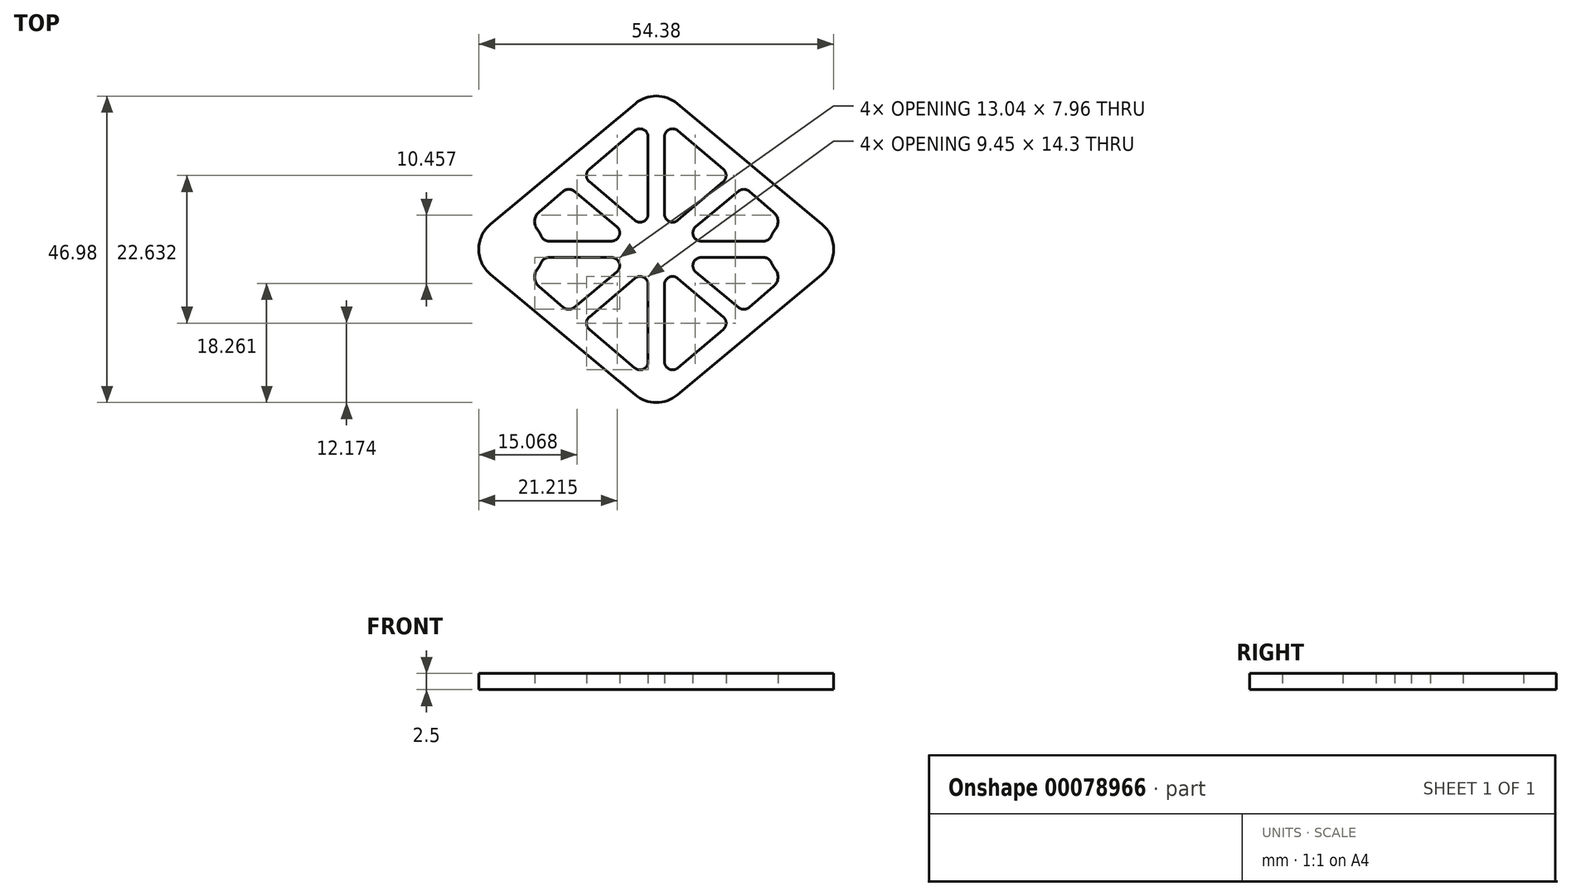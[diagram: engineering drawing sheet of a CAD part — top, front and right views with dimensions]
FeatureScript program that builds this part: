
annotation { "Feature Type Name" : "Feature", "Feature Type Description" : "" }
export const myFeature = defineFeature(function(context is Context, id is Id, definition is map)
    precondition{}
    {
        {
            var Q0;
            Q0=qCreatedBy(makeId("Top.planeOp"),FACE);
            var sketch = newSketch(context, id + "F0", { "sketchPlane" : qUnion([Q0])});
            skLineSegment(sketch, "E0.bottom", {"start": v(30, 25) * mm, "end": v(-30, 25) * mm, "construction": true});
            skLineSegment(sketch, "E0.top", {"start": v(30, -25) * mm, "end": v(-30, -25) * mm, "construction": true});
            skLineSegment(sketch, "E0.left", {"start": v(30, 25) * mm, "end": v(30, -25) * mm, "construction": true});
            skLineSegment(sketch, "E0.right", {"start": v(-30, 25) * mm, "end": v(-30, -25) * mm, "construction": true});
            skPoint(sketch, "E0.middle", {"position": v(0, 0) * mm});
            skPoint(sketch, "E1", {"position": v(0, 25) * mm});
            skPoint(sketch, "E2", {"position": v(0, -25) * mm});
            skPoint(sketch, "E3", {"position": v(30, 0) * mm});
            skPoint(sketch, "E4", {"position": v(-30, 0) * mm});
            skLineSegment(sketch, "E5", {"start": v(-25.4, 3.84) * mm, "end": v(-3.2, 22.33) * mm});
            skLineSegment(sketch, "E6", {"start": v(3.2, 22.33) * mm, "end": v(25.4, 3.84) * mm});
            skLineSegment(sketch, "E7", {"start": v(25.4, -3.84) * mm, "end": v(3.2, -22.33) * mm});
            skLineSegment(sketch, "E8", {"start": v(-3.2, -22.33) * mm, "end": v(-25.4, -3.84) * mm});
            skArc(sketch, "E9.filletArc", {"start": v(3.2, 22.33) * mm, "mid": v(0, 23.5) * mm, "end": v(-3.2, 22.33) * mm});
            skArc(sketch, "E10.filletArc", {"start": v(-25.4, 3.84) * mm, "mid": v(-27.19, 0) * mm, "end": v(-25.4, -3.84) * mm});
            skArc(sketch, "E11.filletArc", {"start": v(-3.2, -22.33) * mm, "mid": v(0, -23.5) * mm, "end": v(3.2, -22.33) * mm});
            skArc(sketch, "E12.filletArc", {"start": v(25.4, -3.84) * mm, "mid": v(27.19, 0) * mm, "end": v(25.4, 3.84) * mm});
            skCircle(sketch, "E13", {"center": v(-22.19, 0) * mm, "radius": 5 * mm});
            skPoint(sketch, "E14", {"position": v(-27.19, 0) * mm});
            skLineSegment(sketch, "E15", {"start": v(-22.19, 0) * mm, "end": v(-27.19, 0) * mm, "construction": true});
            skPoint(sketch, "E16", {"position": v(-24.69, 0) * mm});
            skPoint(sketch, "E17", {"position": v(0, 21) * mm});
            skPoint(sketch, "E18", {"position": v(-17.97, 5.71) * mm});
            skPoint(sketch, "E19", {"position": v(-18.24, 3.07) * mm});
            skArc(sketch, "E20", {"start": v(-17.97, 5.71) * mm, "mid": v(-18.64, 4.45) * mm, "end": v(-18.24, 3.07) * mm});
            skArc(sketch, "E21.MirrorCS", {"start": v(-17.97, -5.71) * mm, "mid": v(-18.64, -4.45) * mm, "end": v(-18.24, -3.07) * mm});
            skCircle(sketch, "E22", {"center": v(-22.19, 0) * mm, "radius": 2.5 * mm});
            skLineSegment(sketch, "E23", {"start": v(0, 0) * mm, "end": v(0, 21) * mm, "construction": true});
            skLineSegment(sketch, "E24.MirrorCS", {"start": v(24.69, 0) * mm, "end": v(0, 21) * mm, "construction": true});
            skArc(sketch, "E25.MirrorCS", {"start": v(17.97, 5.71) * mm, "mid": v(18.64, 4.45) * mm, "end": v(18.24, 3.07) * mm});
            skCircle(sketch, "E26.MirrorC", {"center": v(22.19, 0) * mm, "radius": 5 * mm});
            skCircle(sketch, "E27.MirrorC", {"center": v(22.19, 0) * mm, "radius": 2.5 * mm});
            skArc(sketch, "E28.MirrorCS", {"start": v(17.97, -5.71) * mm, "mid": v(18.64, -4.45) * mm, "end": v(18.24, -3.07) * mm});
            skLineSegment(sketch, "E29.MirrorCS", {"start": v(24.69, 0) * mm, "end": v(0, -21) * mm, "construction": true});
            skLineSegment(sketch, "E30", {"start": v(-17.97, 5.71) * mm, "end": v(0, 21) * mm, "construction": true});
            skLineSegment(sketch, "E31", {"start": v(-17.97, -5.71) * mm, "end": v(0, -21) * mm, "construction": true});
            skPoint(sketch, "E32", {"position": v(12.34, 10.5) * mm});
            skLineSegment(sketch, "E33", {"start": v(17.97, -5.71) * mm, "end": v(0, -21) * mm, "construction": true});
            skLineSegment(sketch, "E34", {"start": v(0, 0) * mm, "end": v(12.34, 10.5) * mm, "construction": true});
            skLineSegment(sketch, "E35", {"start": v(1.25, 19.93) * mm, "end": v(1.25, 0) * mm, "construction": true});
            skLineSegment(sketch, "E36", {"start": v(11.38, 11.32) * mm, "end": v(0, 1.64) * mm, "construction": true});
            skPoint(sketch, "E37", {"position": v(1.25, 2.7) * mm});
            skLineSegment(sketch, "E38", {"start": v(1.25, 5.4) * mm, "end": v(1.25, 17.23) * mm});
            skLineSegment(sketch, "E39", {"start": v(3.3, 4.45) * mm, "end": v(10.26, 10.36) * mm});
            skArc(sketch, "E40.filletArc", {"start": v(1.25, 5.4) * mm, "mid": v(1.98, 4.27) * mm, "end": v(3.3, 4.45) * mm});
            skLineSegment(sketch, "E41", {"start": v(10.26, 12.27) * mm, "end": v(3.3, 18.18) * mm});
            skPoint(sketch, "E42.visualSharp", {"position": v(1.25, 19.93) * mm});
            skArc(sketch, "E42.filletArc", {"start": v(3.3, 18.18) * mm, "mid": v(1.98, 18.36) * mm, "end": v(1.25, 17.23) * mm});
            skPoint(sketch, "E43.visualSharp", {"position": v(11.38, 11.32) * mm});
            skArc(sketch, "E43.filletArc", {"start": v(10.26, 10.36) * mm, "mid": v(10.7, 11.32) * mm, "end": v(10.26, 12.27) * mm});
            skLineSegment(sketch, "E44", {"start": v(0, 0) * mm, "end": v(22.19, 0) * mm, "construction": true});
            skLineSegment(sketch, "E45", {"start": v(0, 1.25) * mm, "end": v(23.22, 1.25) * mm, "construction": true});
            skPoint(sketch, "E46", {"position": v(3.4, 1.25) * mm});
            skLineSegment(sketch, "E47", {"start": v(6.05, 3.46) * mm, "end": v(12.6, 8.92) * mm});
            skLineSegment(sketch, "E48", {"start": v(14.21, 8.9) * mm, "end": v(17.97, 5.71) * mm});
            skLineSegment(sketch, "E49", {"start": v(6.85, 1.25) * mm, "end": v(16.46, 1.25) * mm});
            skArc(sketch, "E50", {"start": v(18.24, 3.07) * mm, "mid": v(17.9, 2.56) * mm, "end": v(17.6, 2) * mm});
            skPoint(sketch, "E51.visualSharp", {"position": v(17.35, 1.25) * mm});
            skArc(sketch, "E51.filletArc", {"start": v(16.46, 1.25) * mm, "mid": v(17.15, 1.45) * mm, "end": v(17.6, 2) * mm});
            skArc(sketch, "E52.filletArc", {"start": v(6.05, 3.46) * mm, "mid": v(5.68, 2.07) * mm, "end": v(6.85, 1.25) * mm});
            skPoint(sketch, "E53.visualSharp", {"position": v(13.4, 9.6) * mm});
            skArc(sketch, "E53.filletArc", {"start": v(14.21, 8.9) * mm, "mid": v(13.4, 9.2) * mm, "end": v(12.6, 8.92) * mm});
            skLineSegment(sketch, "E54.MirrorCS", {"start": v(6.85, -1.25) * mm, "end": v(16.46, -1.25) * mm});
            skArc(sketch, "E55.MirrorCS", {"start": v(6.05, -3.46) * mm, "mid": v(5.68, -2.07) * mm, "end": v(6.85, -1.25) * mm});
            skLineSegment(sketch, "E56.MirrorCS", {"start": v(6.05, -3.46) * mm, "end": v(12.6, -8.92) * mm});
            skPoint(sketch, "E57.MirrorP", {"position": v(13.4, -9.6) * mm});
            skLineSegment(sketch, "E58.MirrorCS", {"start": v(14.21, -8.9) * mm, "end": v(17.97, -5.71) * mm});
            skArc(sketch, "E59.MirrorCS", {"start": v(16.46, -1.25) * mm, "mid": v(17.15, -1.45) * mm, "end": v(17.6, -2) * mm});
            skArc(sketch, "E60.MirrorCS", {"start": v(18.24, -3.07) * mm, "mid": v(17.9, -2.56) * mm, "end": v(17.6, -2) * mm});
            skArc(sketch, "E61.MirrorCS", {"start": v(14.21, -8.9) * mm, "mid": v(13.4, -9.2) * mm, "end": v(12.6, -8.92) * mm});
            skLineSegment(sketch, "E62.MirrorCS", {"start": v(3.3, -4.45) * mm, "end": v(10.26, -10.36) * mm});
            skArc(sketch, "E63.MirrorCS", {"start": v(1.25, -5.4) * mm, "mid": v(1.98, -4.27) * mm, "end": v(3.3, -4.45) * mm});
            skLineSegment(sketch, "E64.MirrorCS", {"start": v(1.25, -5.4) * mm, "end": v(1.25, -17.23) * mm});
            skArc(sketch, "E65.MirrorCS", {"start": v(3.3, -18.18) * mm, "mid": v(1.98, -18.36) * mm, "end": v(1.25, -17.23) * mm});
            skLineSegment(sketch, "E66.MirrorCS", {"start": v(10.26, -12.27) * mm, "end": v(3.3, -18.18) * mm});
            skArc(sketch, "E67.MirrorCS", {"start": v(10.26, -10.36) * mm, "mid": v(10.7, -11.32) * mm, "end": v(10.26, -12.27) * mm});
            skLineSegment(sketch, "E68.MirrorCS", {"start": v(-1.25, 5.4) * mm, "end": v(-1.25, 17.23) * mm});
            skArc(sketch, "E69.MirrorCS", {"start": v(-3.3, 18.18) * mm, "mid": v(-1.98, 18.36) * mm, "end": v(-1.25, 17.23) * mm});
            skLineSegment(sketch, "E70.MirrorCS", {"start": v(-10.26, 12.27) * mm, "end": v(-3.3, 18.18) * mm});
            skArc(sketch, "E71.MirrorCS", {"start": v(-10.26, 10.36) * mm, "mid": v(-10.7, 11.32) * mm, "end": v(-10.26, 12.27) * mm});
            skLineSegment(sketch, "E72.MirrorCS", {"start": v(-3.3, 4.45) * mm, "end": v(-10.26, 10.36) * mm});
            skArc(sketch, "E73.MirrorCS", {"start": v(-1.25, 5.4) * mm, "mid": v(-1.98, 4.27) * mm, "end": v(-3.3, 4.45) * mm});
            skLineSegment(sketch, "E74.MirrorCS", {"start": v(-6.05, 3.46) * mm, "end": v(-12.6, 8.92) * mm});
            skArc(sketch, "E75.MirrorCS", {"start": v(-14.21, 8.9) * mm, "mid": v(-13.4, 9.2) * mm, "end": v(-12.6, 8.92) * mm});
            skLineSegment(sketch, "E76.MirrorCS", {"start": v(-14.21, 8.9) * mm, "end": v(-17.97, 5.71) * mm});
            skArc(sketch, "E77.MirrorCS", {"start": v(-6.05, 3.46) * mm, "mid": v(-5.68, 2.07) * mm, "end": v(-6.85, 1.25) * mm});
            skLineSegment(sketch, "E78.MirrorCS", {"start": v(-6.85, 1.25) * mm, "end": v(-16.46, 1.25) * mm});
            skArc(sketch, "E79.MirrorCS", {"start": v(-16.46, 1.25) * mm, "mid": v(-17.15, 1.45) * mm, "end": v(-17.6, 2) * mm});
            skArc(sketch, "E80.MirrorCS", {"start": v(-18.24, 3.07) * mm, "mid": v(-17.9, 2.56) * mm, "end": v(-17.6, 2) * mm});
            skLineSegment(sketch, "E81.MirrorCS", {"start": v(-3.3, -4.45) * mm, "end": v(-10.26, -10.36) * mm});
            skArc(sketch, "E82.MirrorCS", {"start": v(-10.26, -10.36) * mm, "mid": v(-10.7, -11.32) * mm, "end": v(-10.26, -12.27) * mm});
            skArc(sketch, "E83.MirrorCS", {"start": v(-1.25, -5.4) * mm, "mid": v(-1.98, -4.27) * mm, "end": v(-3.3, -4.45) * mm});
            skLineSegment(sketch, "E84.MirrorCS", {"start": v(-1.25, -5.4) * mm, "end": v(-1.25, -17.23) * mm});
            skArc(sketch, "E85.MirrorCS", {"start": v(-3.3, -18.18) * mm, "mid": v(-1.98, -18.36) * mm, "end": v(-1.25, -17.23) * mm});
            skLineSegment(sketch, "E86.MirrorCS", {"start": v(-10.26, -12.27) * mm, "end": v(-3.3, -18.18) * mm});
            skArc(sketch, "E87.MirrorCS", {"start": v(-6.05, -3.46) * mm, "mid": v(-5.68, -2.07) * mm, "end": v(-6.85, -1.25) * mm});
            skLineSegment(sketch, "E88.MirrorCS", {"start": v(-6.85, -1.25) * mm, "end": v(-16.46, -1.25) * mm});
            skLineSegment(sketch, "E89.MirrorCS", {"start": v(-6.05, -3.46) * mm, "end": v(-12.6, -8.92) * mm});
            skArc(sketch, "E90.MirrorCS", {"start": v(-14.21, -8.9) * mm, "mid": v(-13.4, -9.2) * mm, "end": v(-12.6, -8.92) * mm});
            skArc(sketch, "E91.MirrorCS", {"start": v(-16.46, -1.25) * mm, "mid": v(-17.15, -1.45) * mm, "end": v(-17.6, -2) * mm});
            skLineSegment(sketch, "E92", {"start": v(-17.97, -5.71) * mm, "end": v(-14.21, -8.9) * mm});
            skSolve(sketch);
        }
        {
            var Q0;
            {var subQ6=sQuery(id+"F0.wireOp",EDGE,"E5");Q0=makeQuery(id+"F0.imprint","IMPRINT",FACE,{"disambiguationData":[TD([[makeQuery(id+"F0.imprint","IMPRINT",EDGE,{"derivedFrom":subQ6}),-1.0]])]});}
            var Q1;
            Q1=makeQuery(id+"F0.imprint","IMPRINT",FACE,{"disambiguationData":[TD([[makeQuery(id+"F0.imprint","IMPRINT",EDGE,{"derivedFrom":sQuery(id+"F0.wireOp",EDGE,"E22")}),-1.0]])]});
            var Q2;
            Q2=makeQuery(id+"F0.imprint","IMPRINT",FACE,{"disambiguationData":[TD([[makeQuery(id+"F0.imprint","IMPRINT",EDGE,{"derivedFrom":sQuery(id+"F0.wireOp",EDGE,"E22")}),1.0]])]});
            var Q3;
            Q3=makeQuery(id+"F0.imprint","IMPRINT",FACE,{"disambiguationData":[TD([[makeQuery(id+"F0.imprint","IMPRINT",EDGE,{"derivedFrom":sQuery(id+"F0.wireOp",EDGE,"E27.MirrorC")}),1.0]])]});
            var Q4;
            Q4=makeQuery(id+"F0.imprint","IMPRINT",FACE,{"disambiguationData":[TD([[makeQuery(id+"F0.imprint","IMPRINT",EDGE,{"derivedFrom":sQuery(id+"F0.wireOp",EDGE,"E27.MirrorC")}),-1.0]])]});
            extrude(context, id + "F1", {"entities" : qUnion([Q0, Q1, Q2, Q3, Q4]), "depth" : 2.5 * mm});
        }
    });
